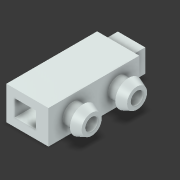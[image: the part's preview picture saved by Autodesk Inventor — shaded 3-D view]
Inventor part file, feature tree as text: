
AUTODESK INVENTOR PART (.ipt)
format: ipt  version: 2020.2 (Build 242310000, 310)  size: 241,152 bytes
history: native  units: mm
features: other x6, extrude x3, loft x2, pattern_linear x1
ambient origin geometry x8: Origin, YZ Plane, XZ Plane, XY Plane, X Axis, Y Axis, Z Axis, Center Point
bodies: Solid1 (feature_tree)
feature tree (12):
  other  "Start Plane"
  other  "End Plane"
  other  "Box Sketch"
  other  "Fitting"
  extrude  "Box"  Depth=3.0mm
  loft  "Loft Start Plane"
  pattern_linear  "Channel Repetition"  Spacing1=60.0deg  [1 undecoded]
  extrude  "Clip Extra Length"  Depth=2.5mm
  extrude  "Connector"  Depth=4.7625mm
  other  "Fitting Sketch"
  loft  "Loft Sketch"
  other  "Edges1"
note: 1 required parameter value undecoded (feature->parameter linkage not recoverable at this tier; creation-order binding heuristic only, values carry confidence <= 0.55)
